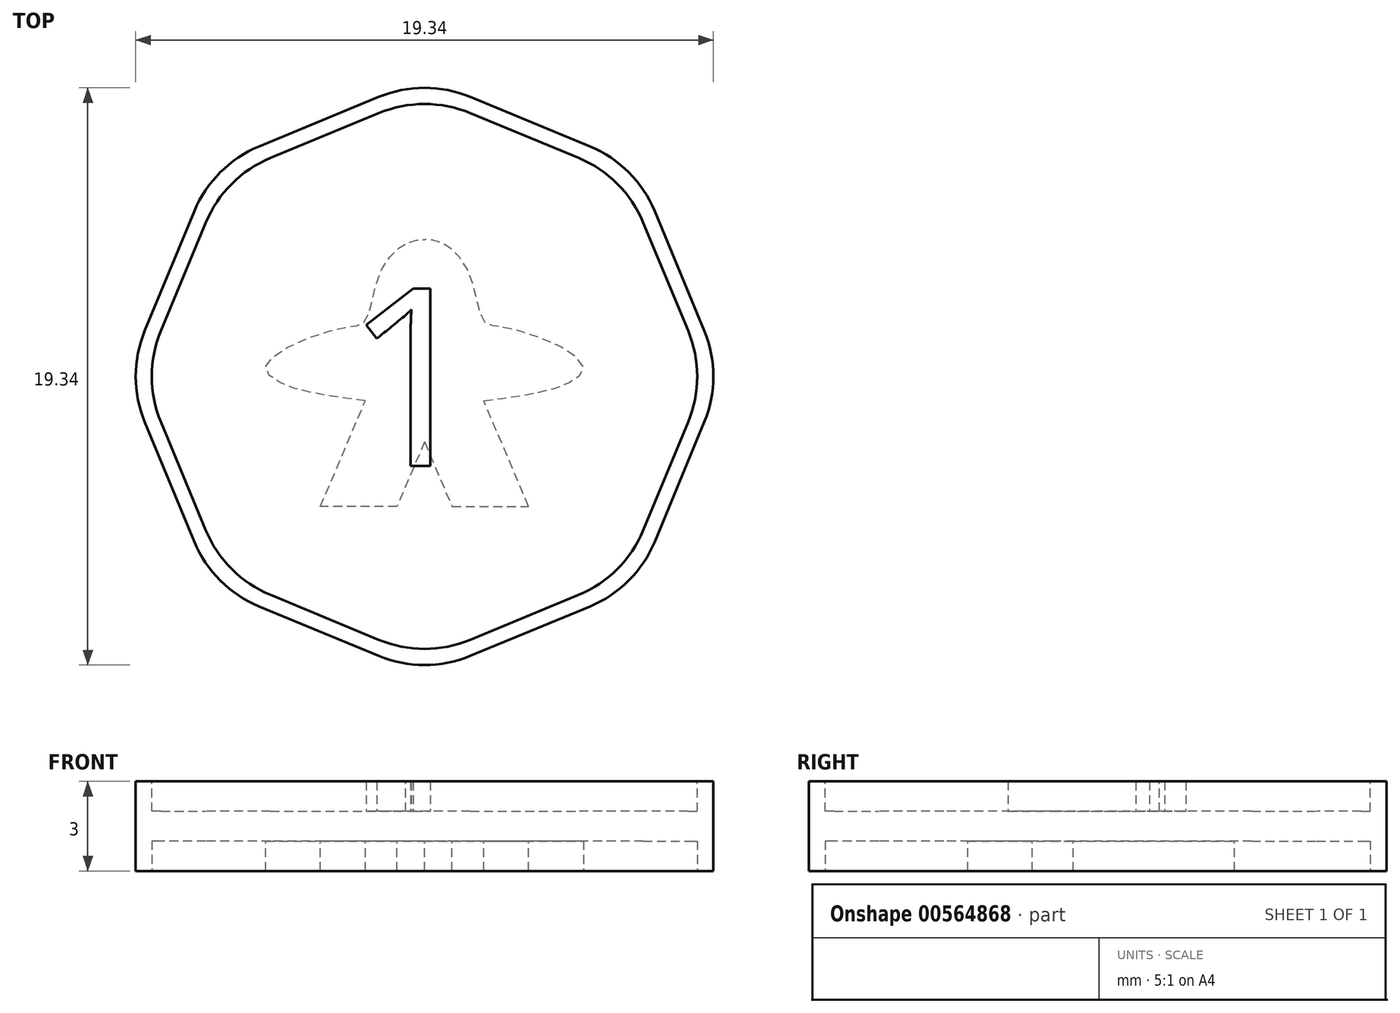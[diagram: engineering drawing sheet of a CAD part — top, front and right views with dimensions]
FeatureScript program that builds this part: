
annotation { "Feature Type Name" : "Feature", "Feature Type Description" : "" }
export const myFeature = defineFeature(function(context is Context, id is Id, definition is map)
    precondition{}
    {
        {
            assignVariable(context, id + "F0", {"name" : "Thickness", "anyValue" : 3});
        }
        {
            assignVariable(context, id + "F1", {"name" : "ImpressionDepth", "anyValue" : 1});
        }
        {
            var Q0;
            Q0=qCreatedBy(makeId("Top.planeOp"),FACE);
            var sketch = newSketch(context, id + "F2", { "sketchPlane" : qUnion([Q0])});
            skCircle(sketch, "E0.cCircle", {"center": v(0, 0) * mm, "radius": 10 * mm, "construction": true});
            skLineSegment(sketch, "E0.0", {"start": v(9.37, -1.53) * mm, "end": v(7.7, -5.54) * mm});
            skLineSegment(sketch, "E0.1", {"start": v(5.54, -7.7) * mm, "end": v(1.53, -9.37) * mm});
            skLineSegment(sketch, "E0.2", {"start": v(-1.53, -9.37) * mm, "end": v(-5.54, -7.7) * mm});
            skLineSegment(sketch, "E0.3", {"start": v(-7.7, -5.54) * mm, "end": v(-9.37, -1.53) * mm});
            skLineSegment(sketch, "E0.4", {"start": v(-9.37, 1.53) * mm, "end": v(-7.7, 5.54) * mm});
            skLineSegment(sketch, "E0.5", {"start": v(-5.54, 7.7) * mm, "end": v(-1.53, 9.37) * mm});
            skLineSegment(sketch, "E0.6", {"start": v(1.53, 9.37) * mm, "end": v(5.54, 7.7) * mm});
            skLineSegment(sketch, "E0.7", {"start": v(7.7, 5.54) * mm, "end": v(9.37, 1.53) * mm});
            skPoint(sketch, "E1.visualSharp", {"position": v(-7.07, 7.07) * mm});
            skArc(sketch, "E1.filletArc", {"start": v(-5.54, 7.7) * mm, "mid": v(-6.84, 6.84) * mm, "end": v(-7.7, 5.54) * mm});
            skPoint(sketch, "E2.visualSharp", {"position": v(0, 10) * mm});
            skArc(sketch, "E2.filletArc", {"start": v(1.53, 9.37) * mm, "mid": v(0, 9.67) * mm, "end": v(-1.53, 9.37) * mm});
            skPoint(sketch, "E3.visualSharp", {"position": v(7.07, 7.07) * mm});
            skArc(sketch, "E3.filletArc", {"start": v(7.7, 5.54) * mm, "mid": v(6.84, 6.84) * mm, "end": v(5.54, 7.7) * mm});
            skPoint(sketch, "E4.visualSharp", {"position": v(10, 0) * mm});
            skArc(sketch, "E4.filletArc", {"start": v(9.37, -1.53) * mm, "mid": v(9.67, 0) * mm, "end": v(9.37, 1.53) * mm});
            skPoint(sketch, "E5.visualSharp", {"position": v(-10, 0) * mm});
            skArc(sketch, "E5.filletArc", {"start": v(-9.37, 1.53) * mm, "mid": v(-9.67, 0) * mm, "end": v(-9.37, -1.53) * mm});
            skPoint(sketch, "E6.visualSharp", {"position": v(-7.07, -7.07) * mm});
            skArc(sketch, "E6.filletArc", {"start": v(-7.7, -5.54) * mm, "mid": v(-6.84, -6.84) * mm, "end": v(-5.54, -7.7) * mm});
            skPoint(sketch, "E7.visualSharp", {"position": v(0, -10) * mm});
            skArc(sketch, "E7.filletArc", {"start": v(-1.53, -9.37) * mm, "mid": v(0, -9.67) * mm, "end": v(1.53, -9.37) * mm});
            skPoint(sketch, "E8.visualSharp", {"position": v(7.07, -7.07) * mm});
            skArc(sketch, "E8.filletArc", {"start": v(5.54, -7.7) * mm, "mid": v(6.84, -6.84) * mm, "end": v(7.7, -5.54) * mm});
            skSolve(sketch);
        }
        {
            var Q0;
            Q0=qSketchRegion(id+"F2",true);
            extrude(context, id + "F3", {"entities" : qUnion([Q0]), "oppositeDirection" : true, "depth" : (getVariable(context, 'Thickness')) * mm});
        }
        {
            var Q0;
            Q0=makeQuery(id+"F3.opExtrude","CAP_FACE",FACE,{"disambiguationData":[OSD([sQuery(id+"F2.wireOp",EDGE,"E0.0"),sQuery(id+"F2.wireOp",EDGE,"E0.1"),sQuery(id+"F2.wireOp",EDGE,"E0.2"),sQuery(id+"F2.wireOp",EDGE,"E0.3"),sQuery(id+"F2.wireOp",EDGE,"E0.4"),sQuery(id+"F2.wireOp",EDGE,"E0.5"),sQuery(id+"F2.wireOp",EDGE,"E0.6"),sQuery(id+"F2.wireOp",EDGE,"E0.7")])],"isStart":true});
            var sketch = newSketch(context, id + "F4", { "sketchPlane" : qUnion([Q0])});
            skLineSegment(sketch, "E9.0", {"start": v(-7.32, -5.16) * mm, "end": v(-8.82, -1.53) * mm});
            skLineSegment(sketch, "E9.1", {"start": v(-1.53, -8.82) * mm, "end": v(-5.16, -7.32) * mm});
            skLineSegment(sketch, "E9.2", {"start": v(-8.82, 1.53) * mm, "end": v(-7.32, 5.16) * mm});
            skLineSegment(sketch, "E9.3", {"start": v(5.16, -7.32) * mm, "end": v(1.53, -8.82) * mm});
            skLineSegment(sketch, "E9.4", {"start": v(-5.16, 7.32) * mm, "end": v(-1.53, 8.82) * mm});
            skLineSegment(sketch, "E9.5", {"start": v(1.53, 8.82) * mm, "end": v(5.16, 7.32) * mm});
            skLineSegment(sketch, "E9.6", {"start": v(7.32, 5.16) * mm, "end": v(8.82, 1.53) * mm});
            skLineSegment(sketch, "E9.7", {"start": v(8.82, -1.53) * mm, "end": v(7.32, -5.16) * mm});
            skPoint(sketch, "E10.visualSharp", {"position": v(-6.69, 6.69) * mm});
            skArc(sketch, "E10.filletArc", {"start": v(-5.16, 7.32) * mm, "mid": v(-6.46, 6.46) * mm, "end": v(-7.32, 5.16) * mm});
            skPoint(sketch, "E11.visualSharp", {"position": v(0, 9.46) * mm});
            skArc(sketch, "E11.filletArc", {"start": v(1.53, 8.82) * mm, "mid": v(0, 9.13) * mm, "end": v(-1.53, 8.82) * mm});
            skPoint(sketch, "E12.visualSharp", {"position": v(6.69, 6.69) * mm});
            skArc(sketch, "E12.filletArc", {"start": v(7.32, 5.16) * mm, "mid": v(6.46, 6.46) * mm, "end": v(5.16, 7.32) * mm});
            skPoint(sketch, "E13.visualSharp", {"position": v(9.46, 0) * mm});
            skArc(sketch, "E13.filletArc", {"start": v(8.82, -1.53) * mm, "mid": v(9.13, 0) * mm, "end": v(8.82, 1.53) * mm});
            skPoint(sketch, "E14.visualSharp", {"position": v(6.69, -6.69) * mm});
            skArc(sketch, "E14.filletArc", {"start": v(5.16, -7.32) * mm, "mid": v(6.46, -6.46) * mm, "end": v(7.32, -5.16) * mm});
            skPoint(sketch, "E15.visualSharp", {"position": v(0, -9.46) * mm});
            skArc(sketch, "E15.filletArc", {"start": v(-1.53, -8.82) * mm, "mid": v(0, -9.13) * mm, "end": v(1.53, -8.82) * mm});
            skPoint(sketch, "E16.visualSharp", {"position": v(-6.69, -6.69) * mm});
            skArc(sketch, "E16.filletArc", {"start": v(-7.32, -5.16) * mm, "mid": v(-6.46, -6.46) * mm, "end": v(-5.16, -7.32) * mm});
            skPoint(sketch, "E17.visualSharp", {"position": v(-9.46, 0) * mm});
            skArc(sketch, "E17.filletArc", {"start": v(-8.82, 1.53) * mm, "mid": v(-9.13, 0) * mm, "end": v(-8.82, -1.53) * mm});
            skSolve(sketch);
        }
        {
            var Q0;
            Q0=qSketchRegion(id+"F4",true);
            extrude(context, id + "F5", {"entities" : qUnion([Q0]), "operationType" : NewBodyOperationType.REMOVE, "oppositeDirection" : true, "depth" : (getVariable(context, 'ImpressionDepth')) * mm});
        }
        {
            var Q0;
            Q0=makeQuery(id+"F3.opExtrude","CAP_FACE",FACE,{"disambiguationData":[OSD([sQuery(id+"F2.wireOp",EDGE,"E0.0"),sQuery(id+"F2.wireOp",EDGE,"E0.1"),sQuery(id+"F2.wireOp",EDGE,"E0.2"),sQuery(id+"F2.wireOp",EDGE,"E0.3"),sQuery(id+"F2.wireOp",EDGE,"E0.4"),sQuery(id+"F2.wireOp",EDGE,"E0.5"),sQuery(id+"F2.wireOp",EDGE,"E0.6"),sQuery(id+"F2.wireOp",EDGE,"E0.7")])],"isStart":false});
            var sketch = newSketch(context, id + "F6", { "sketchPlane" : qUnion([Q0])});
            skLineSegment(sketch, "E18.0", {"start": v(-8.82, -1.53) * mm, "end": v(-7.32, -5.16) * mm});
            skLineSegment(sketch, "E18.1", {"start": v(-7.32, 5.16) * mm, "end": v(-8.82, 1.53) * mm});
            skLineSegment(sketch, "E18.2", {"start": v(-5.16, -7.32) * mm, "end": v(-1.53, -8.82) * mm});
            skLineSegment(sketch, "E18.3", {"start": v(-1.53, 8.82) * mm, "end": v(-5.16, 7.32) * mm});
            skLineSegment(sketch, "E18.4", {"start": v(1.53, -8.82) * mm, "end": v(5.16, -7.32) * mm});
            skLineSegment(sketch, "E18.5", {"start": v(7.32, -5.16) * mm, "end": v(8.82, -1.53) * mm});
            skLineSegment(sketch, "E18.6", {"start": v(8.82, 1.53) * mm, "end": v(7.32, 5.16) * mm});
            skLineSegment(sketch, "E18.7", {"start": v(5.16, 7.32) * mm, "end": v(1.53, 8.82) * mm});
            skPoint(sketch, "E19.visualSharp", {"position": v(-6.69, 6.69) * mm});
            skArc(sketch, "E19.filletArc", {"start": v(-5.16, 7.32) * mm, "mid": v(-6.46, 6.46) * mm, "end": v(-7.32, 5.16) * mm});
            skPoint(sketch, "E20.visualSharp", {"position": v(0, 9.46) * mm});
            skArc(sketch, "E20.filletArc", {"start": v(1.53, 8.82) * mm, "mid": v(0, 9.13) * mm, "end": v(-1.53, 8.82) * mm});
            skPoint(sketch, "E21.visualSharp", {"position": v(6.69, 6.69) * mm});
            skArc(sketch, "E21.filletArc", {"start": v(7.32, 5.16) * mm, "mid": v(6.46, 6.46) * mm, "end": v(5.16, 7.32) * mm});
            skPoint(sketch, "E22.visualSharp", {"position": v(9.46, 0) * mm});
            skArc(sketch, "E22.filletArc", {"start": v(8.82, -1.53) * mm, "mid": v(9.13, 0) * mm, "end": v(8.82, 1.53) * mm});
            skPoint(sketch, "E23.visualSharp", {"position": v(6.69, -6.69) * mm});
            skArc(sketch, "E23.filletArc", {"start": v(5.16, -7.32) * mm, "mid": v(6.46, -6.46) * mm, "end": v(7.32, -5.16) * mm});
            skPoint(sketch, "E24.visualSharp", {"position": v(0, -9.46) * mm});
            skArc(sketch, "E24.filletArc", {"start": v(-1.53, -8.82) * mm, "mid": v(0, -9.13) * mm, "end": v(1.53, -8.82) * mm});
            skPoint(sketch, "E25.visualSharp", {"position": v(-6.69, -6.69) * mm});
            skArc(sketch, "E25.filletArc", {"start": v(-7.32, -5.16) * mm, "mid": v(-6.46, -6.46) * mm, "end": v(-5.16, -7.32) * mm});
            skPoint(sketch, "E26.visualSharp", {"position": v(-9.46, 0) * mm});
            skArc(sketch, "E26.filletArc", {"start": v(-8.82, 1.53) * mm, "mid": v(-9.13, 0) * mm, "end": v(-8.82, -1.53) * mm});
            skSolve(sketch);
        }
        {
            var Q0;
            Q0=qSketchRegion(id+"F6",true);
            extrude(context, id + "F7", {"entities" : qUnion([Q0]), "operationType" : NewBodyOperationType.REMOVE, "oppositeDirection" : true, "depth" : (getVariable(context, 'ImpressionDepth')) * mm});
        }
        {
            var Q0;
            Q0=makeQuery(id+"F5.boolean.opBoolean","COPY",FACE,{"derivedFrom":makeQuery(id+"F5.opExtrude","CAP_FACE",FACE,{"disambiguationData":[OSD([sQuery(id+"F4.wireOp",EDGE,"E9.0"),sQuery(id+"F4.wireOp",EDGE,"E9.1"),sQuery(id+"F4.wireOp",EDGE,"E9.2"),sQuery(id+"F4.wireOp",EDGE,"E9.3"),sQuery(id+"F4.wireOp",EDGE,"E9.4"),sQuery(id+"F4.wireOp",EDGE,"E9.5"),sQuery(id+"F4.wireOp",EDGE,"E9.6"),sQuery(id+"F4.wireOp",EDGE,"E9.7"),sQuery(id+"F4.wireOp",EDGE,"E10.filletArc"),sQuery(id+"F4.wireOp",EDGE,"E11.filletArc"),sQuery(id+"F4.wireOp",EDGE,"E12.filletArc"),sQuery(id+"F4.wireOp",EDGE,"E13.filletArc"),sQuery(id+"F4.wireOp",EDGE,"E14.filletArc"),sQuery(id+"F4.wireOp",EDGE,"E15.filletArc"),sQuery(id+"F4.wireOp",EDGE,"E16.filletArc"),sQuery(id+"F4.wireOp",EDGE,"E17.filletArc")])],"isStart":false})});
            var sketch = newSketch(context, id + "F8", { "sketchPlane" : qUnion([Q0])});
            skText(sketch, "E27", { "text": "1", "fontName": "OpenSans-Regular.ttf"});
            skPoint(sketch, "E28", {"position": v(-1, 0) * mm});
            const initialGuessF8  = {"E27": [-0.00272, -0.003, 1, 0, 0.006]};
            skSetInitialGuess(sketch, initialGuessF8);
            skSolve(sketch);
        }
        {
            var Q0;
            Q0=qSketchRegion(id+"F8",true);
            extrude(context, id + "F9", {"entities" : qUnion([Q0]), "operationType" : NewBodyOperationType.ADD, "depth" : (getVariable(context, 'ImpressionDepth')) * mm});
        }
        {
            var Q0;
            Q0=makeQuery(id+"F7.boolean.opBoolean","COPY",FACE,{"derivedFrom":makeQuery(id+"F7.opExtrude","CAP_FACE",FACE,{"disambiguationData":[OSD([sQuery(id+"F6.wireOp",EDGE,"E18.0"),sQuery(id+"F6.wireOp",EDGE,"E18.1"),sQuery(id+"F6.wireOp",EDGE,"E18.2"),sQuery(id+"F6.wireOp",EDGE,"E18.3"),sQuery(id+"F6.wireOp",EDGE,"E18.4"),sQuery(id+"F6.wireOp",EDGE,"E18.5"),sQuery(id+"F6.wireOp",EDGE,"E18.6"),sQuery(id+"F6.wireOp",EDGE,"E18.7"),sQuery(id+"F6.wireOp",EDGE,"E19.filletArc"),sQuery(id+"F6.wireOp",EDGE,"E20.filletArc"),sQuery(id+"F6.wireOp",EDGE,"E21.filletArc"),sQuery(id+"F6.wireOp",EDGE,"E22.filletArc"),sQuery(id+"F6.wireOp",EDGE,"E23.filletArc"),sQuery(id+"F6.wireOp",EDGE,"E24.filletArc"),sQuery(id+"F6.wireOp",EDGE,"E25.filletArc"),sQuery(id+"F6.wireOp",EDGE,"E26.filletArc")])],"isStart":false})});
            var sketch = newSketch(context, id + "F10", { "sketchPlane" : qUnion([Q0])});
            skLineSegment(sketch, "E29", {"start": v(0, -9.13) * mm, "end": v(0, 9.13) * mm, "construction": true});
            skLineSegment(sketch, "E30", {"start": v(0, 2.19) * mm, "end": v(-0.92, 4.36) * mm});
            skLineSegment(sketch, "E31", {"start": v(-0.92, 4.36) * mm, "end": v(-3.49, 4.36) * mm});
            skLineSegment(sketch, "E32", {"start": v(-3.49, 4.36) * mm, "end": v(-1.99, 0.82) * mm});
            skLineSegment(sketch, "E33.MirrorCS", {"start": v(0, 2.19) * mm, "end": v(0.92, 4.36) * mm});
            skLineSegment(sketch, "E34.MirrorCS", {"start": v(3.49, 4.36) * mm, "end": v(1.99, 0.82) * mm});
            skLineSegment(sketch, "E35.MirrorCS", {"start": v(0.92, 4.36) * mm, "end": v(3.49, 4.36) * mm});
            skFitSpline(sketch, "E36", {"points": [v(-1.99, 0.82) * mm, v(-4.54, 0.33) * mm, v(-5.3, -0.38) * mm, v(-2.81, -1.62) * mm, v(-1.99, -1.86) * mm, v(-1.48, -3.48) * mm, v(-0.56, -4.48) * mm, v(0, -4.58) * mm], "startDerivative": vector(-13.78, -2.1) * mm, "endDerivative": vector(6.01, 0) * mm});
            skFitSpline(sketch, "E37.MirrorCS", {"points": [v(1.99, 0.82) * mm, v(4.54, 0.33) * mm, v(5.3, -0.38) * mm, v(2.81, -1.62) * mm, v(1.99, -1.86) * mm, v(1.48, -3.48) * mm, v(0.56, -4.48) * mm, v(0, -4.58) * mm], "startDerivative": vector(13.78, -2.1) * mm, "endDerivative": vector(-6.01, 0) * mm});
            skPoint(sketch, "E38", {"position": v(0, 0) * mm});
            skSolve(sketch);
        }
        {
            var Q0;
            Q0=qSketchRegion(id+"F10",true);
            extrude(context, id + "F11", {"entities" : qUnion([Q0]), "operationType" : NewBodyOperationType.ADD, "depth" : (getVariable(context, 'ImpressionDepth')) * mm});
        }
    });
